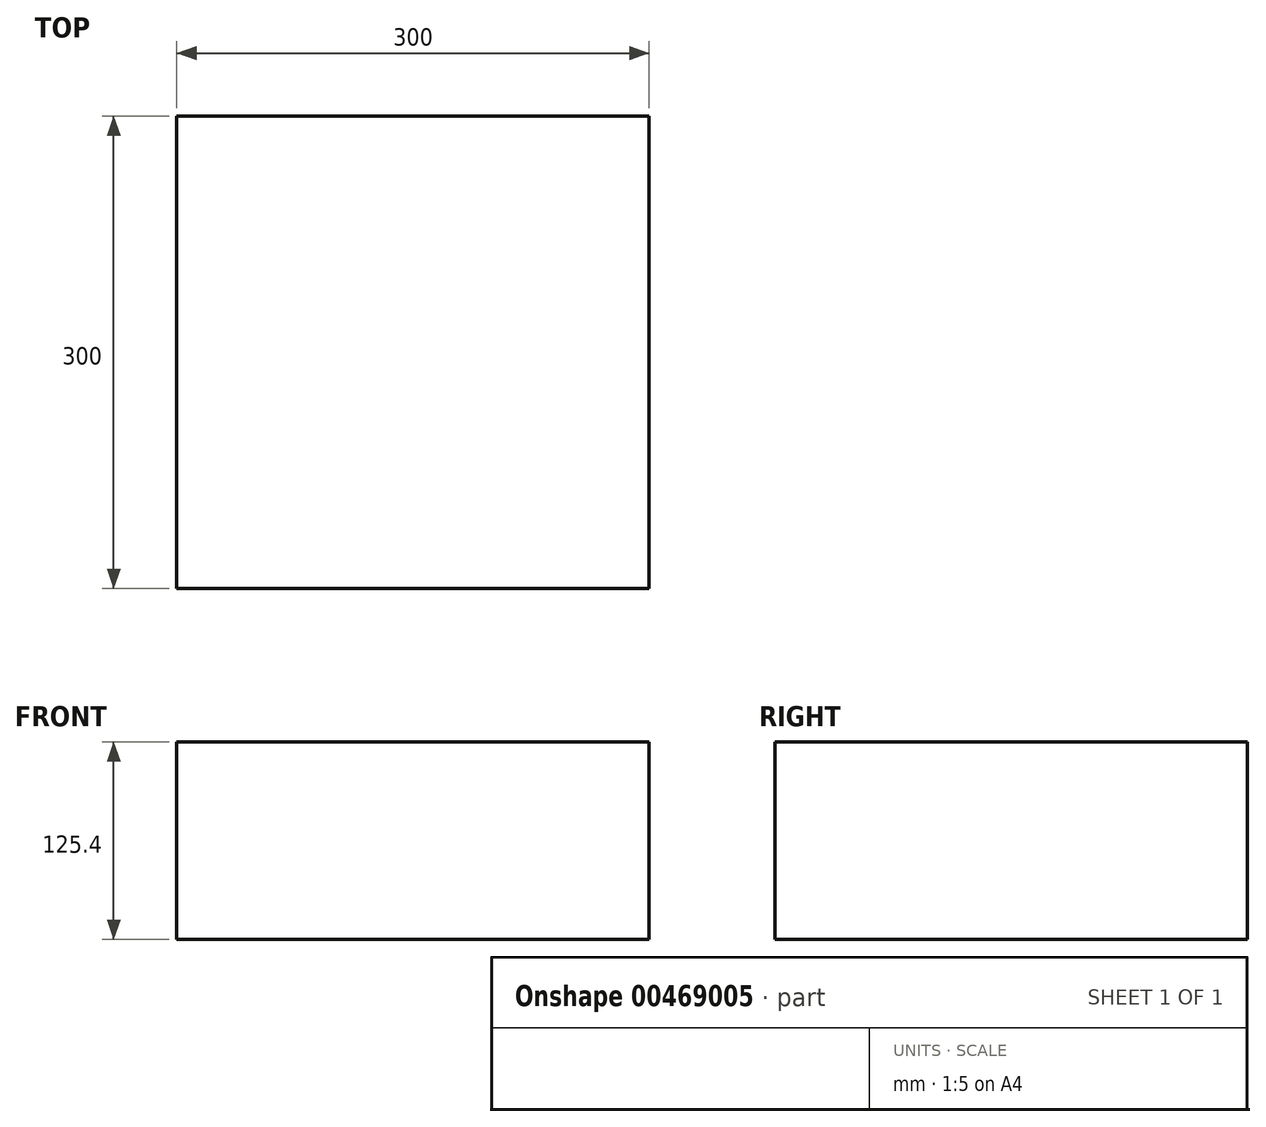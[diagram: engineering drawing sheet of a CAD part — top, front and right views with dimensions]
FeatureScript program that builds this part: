
annotation { "Feature Type Name" : "Feature", "Feature Type Description" : "" }
export const myFeature = defineFeature(function(context is Context, id is Id, definition is map)
    precondition{}
    {
        {
            var Q0;
            Q0=qCreatedBy(makeId("Top.planeOp"),FACE);
            var sketch = newSketch(context, id + "F0", { "sketchPlane" : qUnion([Q0])});
            skLineSegment(sketch, "E0.bottom", {"start": v(-150, -150) * mm, "end": v(150, -150) * mm});
            skLineSegment(sketch, "E0.top", {"start": v(-150, 150) * mm, "end": v(150, 150) * mm});
            skLineSegment(sketch, "E0.left", {"start": v(-150, -150) * mm, "end": v(-150, 150) * mm});
            skLineSegment(sketch, "E0.right", {"start": v(150, -150) * mm, "end": v(150, 150) * mm});
            skPoint(sketch, "E0.middle", {"position": v(0, 0) * mm});
            skSolve(sketch);
        }
        {
            var Q0;
            Q0=makeQuery(id+"F0.imprint","IMPRINT",FACE,{"disambiguationData":[TD([[makeQuery(id+"F0.imprint","IMPRINT",EDGE,{"derivedFrom":sQuery(id+"F0.wireOp",EDGE,"E0.bottom")}),1.0]])]});
            extrude(context, id + "F1", {"entities" : qUnion([Q0]), "depth" : 100 * mm, "hasSecondDirection" : true, "secondDirectionOppositeDirection" : true, "secondDirectionDepth" : 25.4 * mm});
        }
    });
